# Revit family: E-921
name_source: partatom
category: Plumbing Fixtures
revit_build: Autodesk Revit 2015 (Build: 20140606_1530(x64)
units: mm (PartAtom-declared; Revit-internal decimal feet)

## types (1)
- E-921
    Accesorios = Contra de Push. Inserto para Rebosadero. Herramienta para Sujeción. Llave para Aireador. Llave para Mantenimiento. Llave Allen 5/64".
    Características del Producto = Monomando para lavabo con desage de push
    Cuerpo de Latón = Brass
    Default Elevation = 35"
    Description = Alika E-921
    Ficha Técnica = http://www.helvex.com
    Garantía = El producto HELVEX está garantizado como libre de defectos en materiales y procesos de fabricación. El producto HELVEX está garantizado, en lo que se refiere a los acabados; por un periodo de 10 años en los acabados cromo y duravex, y por 2 años en acabados diferentes al cromo, a partir de la fecha de compra indicada en la factura.
    Guía de Instalación = http://www.helvex.com
    Instalación = Conexión ½ - 14 NPSM
    Manufacturer = HELVEX S.A. de C.V.
    Model = E-921
    Operación = Para abrir y cerrar el flujo de agua, desplace el maneral hacia atrás, para regular la temperatura desplace el maneral en sentido antihorario para más caliente y para más fría desplace en sentido horario.
    Presión Máxima de Trabajo = 85.3 psi
    Presión Mínima de Trabajo = 8.5 psi
    Total Depth = 9"
    Total Height = 10"
    Total Width = 4"
    Type Comments = Monomando para Lavabo Alto con Desage de Push
    URL = http://www.helvex.com

## geometry (parser evidence)
native form markers: Sweep x3
no freeform markers — native parametric forms only
